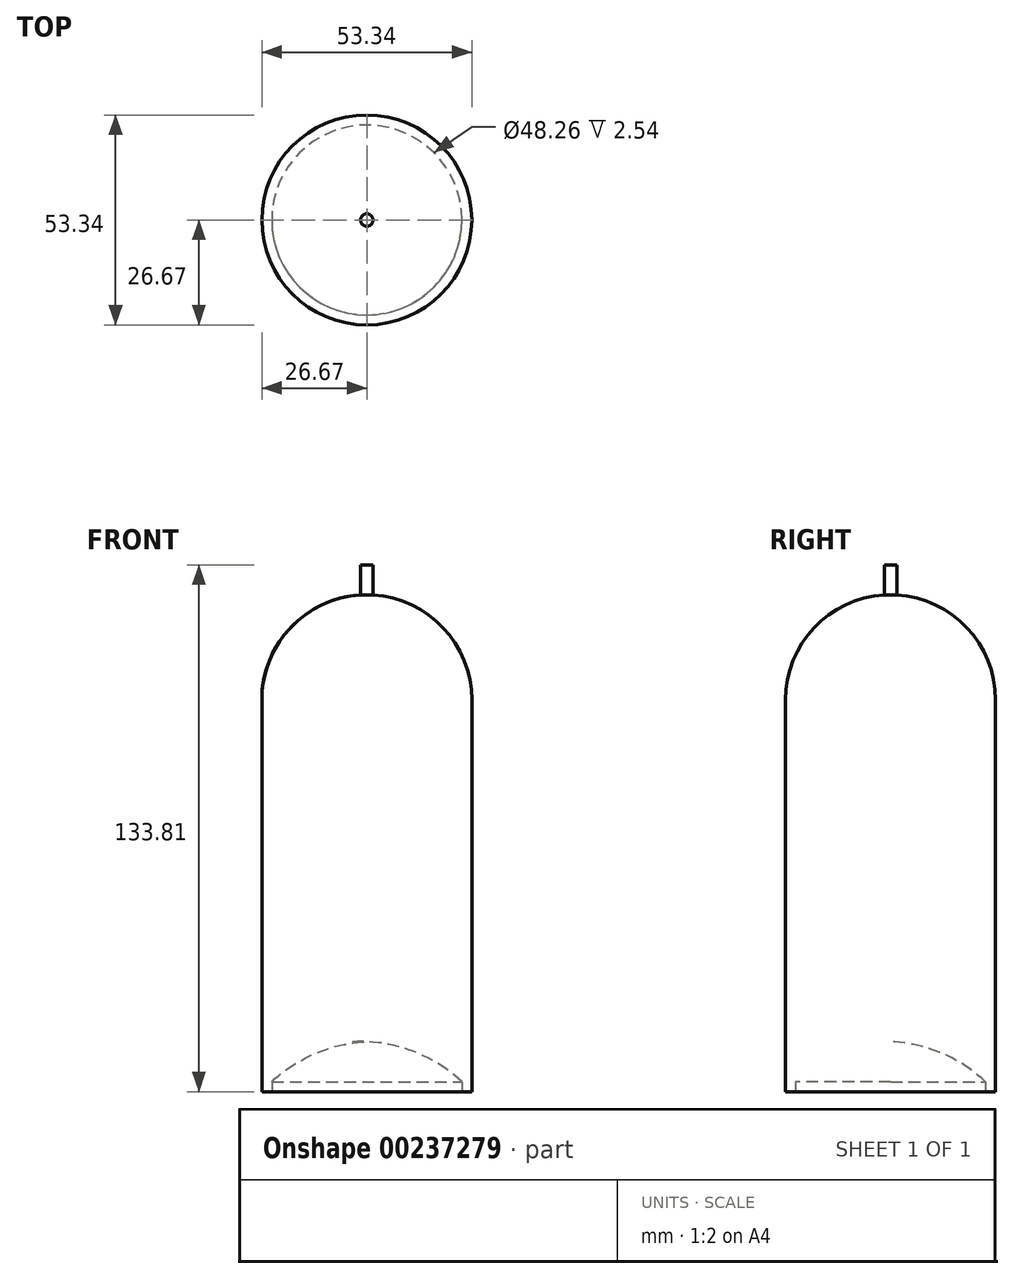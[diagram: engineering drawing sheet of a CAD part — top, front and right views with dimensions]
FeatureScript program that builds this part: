
annotation { "Feature Type Name" : "Feature", "Feature Type Description" : "" }
export const myFeature = defineFeature(function(context is Context, id is Id, definition is map)
    precondition{}
    {
        {
            var Q0;
            Q0=qCreatedBy(makeId("Front.planeOp"),FACE);
            var sketch = newSketch(context, id + "F0", { "sketchPlane" : qUnion([Q0])});
            skLineSegment(sketch, "E0", {"start": v(-26.67, 0) * mm, "end": v(-26.67, 99.57) * mm});
            skArc(sketch, "E1", {"start": v(-26.67, 99.57) * mm, "mid": v(-19.41, 117.86) * mm, "end": v(-1.59, 126.2) * mm});
            skLineSegment(sketch, "E2", {"start": v(-1.59, 126.2) * mm, "end": v(-1.59, 133.81) * mm});
            skLineSegment(sketch, "E3", {"start": v(-26.67, 0) * mm, "end": v(-24.13, 0) * mm});
            skLineSegment(sketch, "E4", {"start": v(0, 12.7) * mm, "end": v(0, 133.81) * mm});
            skLineSegment(sketch, "E5", {"start": v(0, 133.81) * mm, "end": v(-1.59, 133.81) * mm});
            skLineSegment(sketch, "E6", {"start": v(-24.13, 0) * mm, "end": v(-24.13, 2.54) * mm});
            skArc(sketch, "E7", {"start": v(0, 12.7) * mm, "mid": v(-12.97, 9.76) * mm, "end": v(-24.13, 2.54) * mm});
            skSolve(sketch);
        }
        {
            var Q0;
            Q0=makeQuery(id+"F0.imprint","IMPRINT",FACE,{"disambiguationData":[TD([[makeQuery(id+"F0.imprint","IMPRINT",EDGE,{"derivedFrom":sQuery(id+"F0.wireOp",EDGE,"E0")}),-1.0]])]});
            var Q1;
            Q1=sQuery(id+"F0.wireOp",EDGE,"E4");
            revolve(context, id + "F1", {"entities" : qUnion([Q0]), "axis" : qUnion([Q1]), "revolveType" : RevolveType.FULL});
        }
        {
            var Q0;
            Q0=qCreatedBy(makeId("Front.planeOp"),FACE);
            var sketch = newSketch(context, id + "F2", { "sketchPlane" : qUnion([Q0])});
            skLineSegment(sketch, "E8", {"start": v(0, 133.81) * mm, "end": v(-9.52, 133.81) * mm});
            skLineSegment(sketch, "E9", {"start": v(-9.53, 133.81) * mm, "end": v(-9.53, 121.11) * mm});
            skLineSegment(sketch, "E10", {"start": v(-9.52, 121.11) * mm, "end": v(-12.07, 121.11) * mm});
            skLineSegment(sketch, "E11", {"start": v(-12.07, 121.11) * mm, "end": v(-12.07, 138.9) * mm});
            skLineSegment(sketch, "E12", {"start": v(-12.07, 138.9) * mm, "end": v(-1.59, 138.9) * mm});
            skLineSegment(sketch, "E13", {"start": v(-1.59, 138.9) * mm, "end": v(-1.59, 151.6) * mm});
            skLineSegment(sketch, "E14", {"start": v(-1.59, 151.6) * mm, "end": v(0, 151.6) * mm});
            skLineSegment(sketch, "E15", {"start": v(0, 151.6) * mm, "end": v(0, 133.81) * mm});
            skSolve(sketch);
        }
        {
            var Q0;
            Q0=makeQuery(id+"F2.imprint","IMPRINT",FACE,{"disambiguationData":[TD([[makeQuery(id+"F2.imprint","IMPRINT",EDGE,{"derivedFrom":sQuery(id+"F2.wireOp",EDGE,"E8")}),-1.0]])]});
            var Q1;
            Q1=sQuery(id+"F2.wireOp",EDGE,"E15");
            revolve(context, id + "F3", {"entities" : qUnion([Q0]), "axis" : qUnion([Q1]), "revolveType" : RevolveType.FULL});
        }
        {
            var Q0;
            Q0=makeQuery(id+"F3.opRevolve","SWEPT_BODY",BODY,{"disambiguationData":[OSD([sQuery(id+"F2.wireOp",EDGE,"E8"),sQuery(id+"F2.wireOp",EDGE,"E9"),sQuery(id+"F2.wireOp",EDGE,"E10"),sQuery(id+"F2.wireOp",EDGE,"E11"),sQuery(id+"F2.wireOp",EDGE,"E12"),sQuery(id+"F2.wireOp",EDGE,"E13"),sQuery(id+"F2.wireOp",EDGE,"E14"),sQuery(id+"F2.wireOp",EDGE,"E15")])]});
            deleteBodies(context, id + "F4", {"entities" : qUnion([Q0])});
        }
    });
